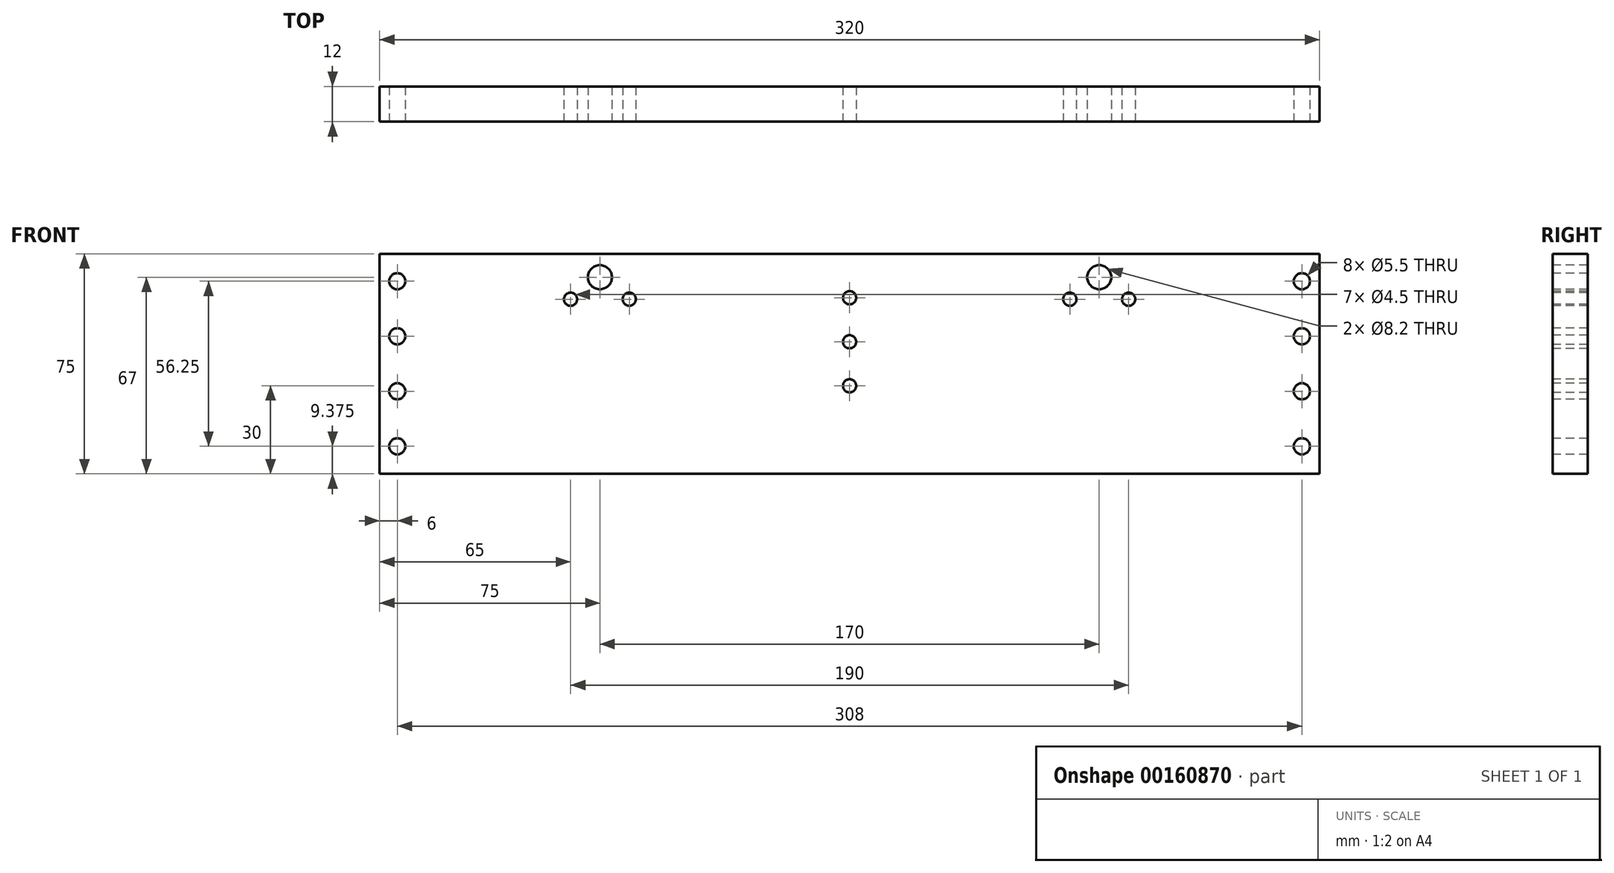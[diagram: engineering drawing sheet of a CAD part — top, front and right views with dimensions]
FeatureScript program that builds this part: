
annotation { "Feature Type Name" : "Feature", "Feature Type Description" : "" }
export const myFeature = defineFeature(function(context is Context, id is Id, definition is map)
    precondition{}
    {
        {
            var Q0;
            Q0=qCreatedBy(makeId("Front.planeOp"),FACE);
            var sketch = newSketch(context, id + "F0", { "sketchPlane" : qUnion([Q0])});
            skLineSegment(sketch, "E0.bottom", {"start": v(-160, 37.5) * mm, "end": v(160, 37.5) * mm});
            skLineSegment(sketch, "E0.top", {"start": v(-160, -37.5) * mm, "end": v(160, -37.5) * mm});
            skLineSegment(sketch, "E0.left", {"start": v(-160, 37.5) * mm, "end": v(-160, -37.5) * mm});
            skLineSegment(sketch, "E0.right", {"start": v(160, 37.5) * mm, "end": v(160, -37.5) * mm});
            skPoint(sketch, "E1", {"position": v(-160, 0) * mm});
            skPoint(sketch, "E2", {"position": v(0, 37.5) * mm});
            skCircle(sketch, "E3", {"center": v(0, 7.5) * mm, "radius": 2.25 * mm});
            skCircle(sketch, "E4", {"center": v(0, 22.5) * mm, "radius": 2.25 * mm});
            skCircle(sketch, "E5", {"center": v(0, -7.5) * mm, "radius": 2.25 * mm});
            skCircle(sketch, "E6", {"center": v(85, 29.5) * mm, "radius": 4.1 * mm});
            skCircle(sketch, "E7", {"center": v(95, 22) * mm, "radius": 2.25 * mm});
            skLineSegment(sketch, "E8", {"start": v(85, 29.5) * mm, "end": v(85, 8.7) * mm, "construction": true});
            skCircle(sketch, "E9.MirrorC", {"center": v(75, 22) * mm, "radius": 2.25 * mm});
            skCircle(sketch, "E10.MirrorC", {"center": v(-75, 22) * mm, "radius": 2.25 * mm});
            skCircle(sketch, "E11.MirrorC", {"center": v(-95, 22) * mm, "radius": 2.25 * mm});
            skCircle(sketch, "E12.MirrorC", {"center": v(-85, 29.5) * mm, "radius": 4.1 * mm});
            skCircle(sketch, "E13", {"center": v(-154, 28.13) * mm, "radius": 2.75 * mm});
            skLineSegment(sketch, "E14", {"start": v(-160, 37.5) * mm, "end": v(-160, 0) * mm, "construction": true});
            skCircle(sketch, "E15.1.0.0", {"center": v(-154, 9.38) * mm, "radius": 2.75 * mm});
            skCircle(sketch, "E15.2.0.0", {"center": v(-154, -9.37) * mm, "radius": 2.75 * mm});
            skCircle(sketch, "E15.3.0.0", {"center": v(-154, -28.12) * mm, "radius": 2.75 * mm});
            skLineSegment(sketch, "E15.direction1", {"start": v(-154, 28.13) * mm, "end": v(-154, 9.38) * mm, "construction": true});
            skCircle(sketch, "E16.MirrorC", {"center": v(154, 28.13) * mm, "radius": 2.75 * mm});
            skCircle(sketch, "E17.MirrorC", {"center": v(154, 9.38) * mm, "radius": 2.75 * mm});
            skCircle(sketch, "E18.MirrorC", {"center": v(154, -9.37) * mm, "radius": 2.75 * mm});
            skCircle(sketch, "E19.MirrorC", {"center": v(154, -28.12) * mm, "radius": 2.75 * mm});
            skSolve(sketch);
        }
        {
            var Q0;
            Q0 = qSketchRegion(id + "F0", true);
            extrude(context, id + "F1", {"entities" : qUnion([Q0]), "oppositeDirection" : true, "depth" : 12 * mm});
        }
    });
